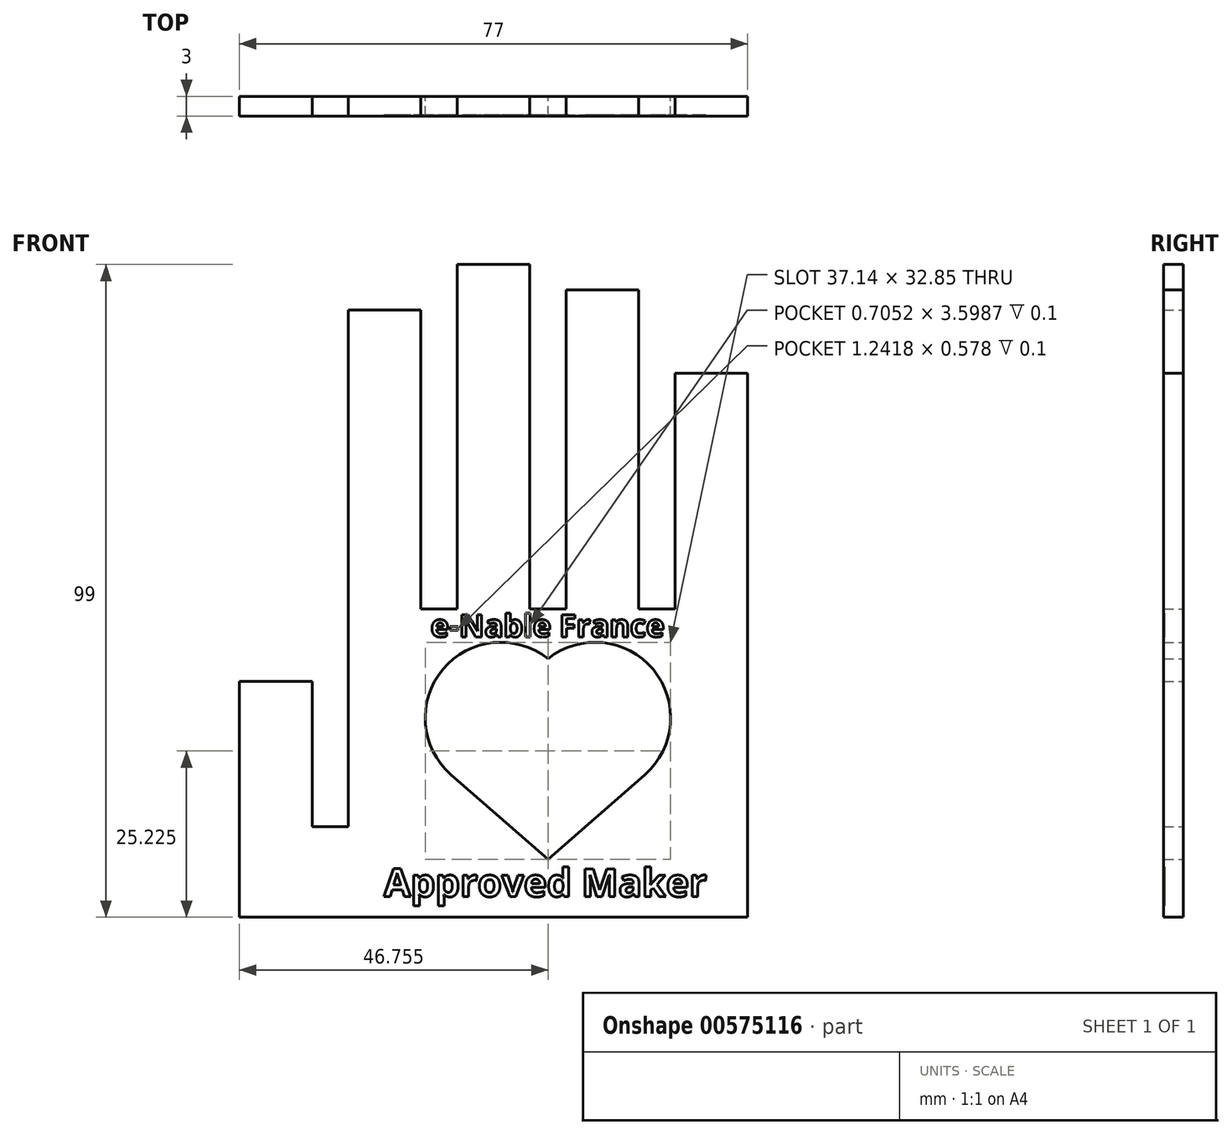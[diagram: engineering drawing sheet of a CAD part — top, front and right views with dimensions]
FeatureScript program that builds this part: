
annotation { "Feature Type Name" : "Feature", "Feature Type Description" : "" }
export const myFeature = defineFeature(function(context is Context, id is Id, definition is map)
    precondition{}
    {
        {
            var Q0;
            Q0=qCreatedBy(makeId("Front.planeOp"),FACE);
            var sketch = newSketch(context, id + "F0", { "sketchPlane" : qUnion([Q0])});
            skLineSegment(sketch, "E0", {"start": v(-37.6, -22.52) * mm, "end": v(-26.6, -22.52) * mm});
            skLineSegment(sketch, "E1", {"start": v(-26.6, -22.52) * mm, "end": v(-26.6, -44.52) * mm});
            skLineSegment(sketch, "E2", {"start": v(-26.6, -44.52) * mm, "end": v(-21.1, -44.52) * mm});
            skLineSegment(sketch, "E3", {"start": v(-21.1, -44.52) * mm, "end": v(-21.1, 33.86) * mm});
            skLineSegment(sketch, "E4", {"start": v(-21.1, 33.86) * mm, "end": v(-10.1, 33.86) * mm});
            skLineSegment(sketch, "E5", {"start": v(-10.1, 33.86) * mm, "end": v(-10.1, -11.52) * mm});
            skLineSegment(sketch, "E6", {"start": v(-10.1, -11.52) * mm, "end": v(-4.6, -11.52) * mm});
            skLineSegment(sketch, "E7", {"start": v(-4.6, -11.52) * mm, "end": v(-4.6, 40.73) * mm});
            skLineSegment(sketch, "E8", {"start": v(-4.6, 40.73) * mm, "end": v(6.4, 40.73) * mm});
            skLineSegment(sketch, "E9", {"start": v(6.4, 40.73) * mm, "end": v(6.4, -11.52) * mm});
            skLineSegment(sketch, "E10", {"start": v(6.4, -11.52) * mm, "end": v(11.9, -11.52) * mm});
            skLineSegment(sketch, "E11", {"start": v(11.9, -11.52) * mm, "end": v(11.9, 36.88) * mm});
            skLineSegment(sketch, "E12", {"start": v(11.9, 36.88) * mm, "end": v(22.9, 36.88) * mm});
            skLineSegment(sketch, "E13", {"start": v(22.9, 36.88) * mm, "end": v(22.9, -11.52) * mm});
            skLineSegment(sketch, "E14", {"start": v(22.9, -11.52) * mm, "end": v(28.4, -11.52) * mm});
            skLineSegment(sketch, "E15", {"start": v(28.4, -11.52) * mm, "end": v(28.4, 24.23) * mm});
            skLineSegment(sketch, "E16", {"start": v(28.4, 24.23) * mm, "end": v(39.4, 24.23) * mm});
            skLineSegment(sketch, "E17", {"start": v(39.4, 24.23) * mm, "end": v(39.4, -58.27) * mm});
            skLineSegment(sketch, "E18", {"start": v(39.4, -58.27) * mm, "end": v(-37.6, -58.27) * mm});
            skLineSegment(sketch, "E19", {"start": v(-37.6, -58.27) * mm, "end": v(-37.6, -22.52) * mm});
            skArc(sketch, "E20", {"start": v(9.15, -19.07) * mm, "mid": v(-6.78, -20.67) * mm, "end": v(-5.53, -36.64) * mm});
            skLineSegment(sketch, "E21", {"start": v(-5.53, -36.64) * mm, "end": v(9.15, -49.47) * mm});
            skLineSegment(sketch, "E22", {"start": v(9.15, 12.3) * mm, "end": v(9.15, -11.67) * mm, "construction": true});
            skArc(sketch, "E23.MirrorCS", {"start": v(9.15, -19.07) * mm, "mid": v(25.1, -20.67) * mm, "end": v(23.84, -36.64) * mm});
            skLineSegment(sketch, "E24.MirrorCS", {"start": v(23.84, -36.64) * mm, "end": v(9.15, -49.47) * mm});
            skSolve(sketch);
        }
        {
            var Q0;
            Q0=makeQuery(id+"F0.imprint","IMPRINT",FACE,{"disambiguationData":[TD([[makeQuery(id+"F0.imprint","IMPRINT",EDGE,{"derivedFrom":sQuery(id+"F0.wireOp",EDGE,"E0")}),-1.0]])]});
            extrude(context, id + "F1", {"entities" : qUnion([Q0]), "depth" : 3 * mm, "offsetDistance" : 25 * mm});
        }
        {
            var Q0;
            Q0=makeQuery(id+"F1.opExtrude","CAP_FACE",FACE,{"disambiguationData":[OSD([sQuery(id+"F0.wireOp",EDGE,"E0"),sQuery(id+"F0.wireOp",EDGE,"E1"),sQuery(id+"F0.wireOp",EDGE,"E2"),sQuery(id+"F0.wireOp",EDGE,"E3"),sQuery(id+"F0.wireOp",EDGE,"E4"),sQuery(id+"F0.wireOp",EDGE,"E5"),sQuery(id+"F0.wireOp",EDGE,"E6"),sQuery(id+"F0.wireOp",EDGE,"E7"),sQuery(id+"F0.wireOp",EDGE,"E8"),sQuery(id+"F0.wireOp",EDGE,"E9"),sQuery(id+"F0.wireOp",EDGE,"E10"),sQuery(id+"F0.wireOp",EDGE,"E11"),sQuery(id+"F0.wireOp",EDGE,"E12"),sQuery(id+"F0.wireOp",EDGE,"E13"),sQuery(id+"F0.wireOp",EDGE,"E14"),sQuery(id+"F0.wireOp",EDGE,"E15"),sQuery(id+"F0.wireOp",EDGE,"E16"),sQuery(id+"F0.wireOp",EDGE,"E17"),sQuery(id+"F0.wireOp",EDGE,"E18"),sQuery(id+"F0.wireOp",EDGE,"E19"),sQuery(id+"F0.wireOp",EDGE,"E20"),sQuery(id+"F0.wireOp",EDGE,"E21"),sQuery(id+"F0.wireOp",EDGE,"E23.MirrorCS"),sQuery(id+"F0.wireOp",EDGE,"E24.MirrorCS")])],"isStart":false});
            var sketch = newSketch(context, id + "F2", { "sketchPlane" : qUnion([Q0])});
            skText(sketch, "E25", { "text": "e-Nable France", "fontName": "NotoSans-Bold.ttf"});
            skText(sketch, "E26", { "text": "Approved Maker\n", "fontName": "NotoSans-Bold.ttf"});
            const initialGuessF2  = {"E25": [-0.00863, -0.01575, 1, 0, 0.00341], "E26": [-0.01573, -0.05514, 1, 0, 0.00425]};
            skSetInitialGuess(sketch, initialGuessF2);
            skSolve(sketch);
        }
        {
            var Q0;
            Q0=makeQuery(id+"F2.imprint","IMPRINT",FACE,{"disambiguationData":[TD([[makeQuery(id+"F2.imprint","IMPRINT",EDGE,{"derivedFrom":sQuery(id+"F2.wireOp",EDGE,"E25.sketch_text.stroke-0")}),-1.0]])]});
            var Q1;
            Q1=makeQuery(id+"F2.imprint","IMPRINT",FACE,{"disambiguationData":[TD([[makeQuery(id+"F2.imprint","IMPRINT",EDGE,{"derivedFrom":sQuery(id+"F2.wireOp",EDGE,"E25.sketch_text.stroke-20")}),-1.0]])]});
            var Q2;
            Q2=makeQuery(id+"F2.imprint","IMPRINT",FACE,{"disambiguationData":[TD([[makeQuery(id+"F2.imprint","IMPRINT",EDGE,{"derivedFrom":sQuery(id+"F2.wireOp",EDGE,"E25.sketch_text.stroke-24")}),-1.0]])]});
            var Q3;
            Q3=makeQuery(id+"F2.imprint","IMPRINT",FACE,{"disambiguationData":[TD([[makeQuery(id+"F2.imprint","IMPRINT",EDGE,{"derivedFrom":sQuery(id+"F2.wireOp",EDGE,"E25.sketch_text.stroke-38")}),-1.0]])]});
            var Q4;
            Q4=makeQuery(id+"F2.imprint","IMPRINT",FACE,{"disambiguationData":[TD([[makeQuery(id+"F2.imprint","IMPRINT",EDGE,{"derivedFrom":sQuery(id+"F2.wireOp",EDGE,"E25.sketch_text.stroke-63")}),-1.0]])]});
            var Q5;
            Q5=makeQuery(id+"F2.imprint","IMPRINT",FACE,{"disambiguationData":[TD([[makeQuery(id+"F2.imprint","IMPRINT",EDGE,{"derivedFrom":sQuery(id+"F2.wireOp",EDGE,"E25.sketch_text.stroke-86")}),-1.0]])]});
            var Q6;
            Q6=makeQuery(id+"F2.imprint","IMPRINT",FACE,{"disambiguationData":[TD([[makeQuery(id+"F2.imprint","IMPRINT",EDGE,{"derivedFrom":sQuery(id+"F2.wireOp",EDGE,"E25.sketch_text.stroke-90")}),-1.0]])]});
            var Q7;
            Q7=makeQuery(id+"F2.imprint","IMPRINT",FACE,{"disambiguationData":[TD([[makeQuery(id+"F2.imprint","IMPRINT",EDGE,{"derivedFrom":sQuery(id+"F2.wireOp",EDGE,"E25.sketch_text.stroke-110")}),-1.0]])]});
            var Q8;
            Q8=makeQuery(id+"F2.imprint","IMPRINT",FACE,{"disambiguationData":[TD([[makeQuery(id+"F2.imprint","IMPRINT",EDGE,{"derivedFrom":sQuery(id+"F2.wireOp",EDGE,"E25.sketch_text.stroke-120")}),-1.0]])]});
            var Q9;
            Q9=makeQuery(id+"F2.imprint","IMPRINT",FACE,{"disambiguationData":[TD([[makeQuery(id+"F2.imprint","IMPRINT",EDGE,{"derivedFrom":sQuery(id+"F2.wireOp",EDGE,"E25.sketch_text.stroke-133")}),-1.0]])]});
            var Q10;
            Q10=makeQuery(id+"F2.imprint","IMPRINT",FACE,{"disambiguationData":[TD([[makeQuery(id+"F2.imprint","IMPRINT",EDGE,{"derivedFrom":sQuery(id+"F2.wireOp",EDGE,"E25.sketch_text.stroke-158")}),-1.0]])]});
            var Q11;
            Q11=makeQuery(id+"F2.imprint","IMPRINT",FACE,{"disambiguationData":[TD([[makeQuery(id+"F2.imprint","IMPRINT",EDGE,{"derivedFrom":sQuery(id+"F2.wireOp",EDGE,"E25.sketch_text.stroke-175")}),-1.0]])]});
            var Q12;
            Q12=makeQuery(id+"F2.imprint","IMPRINT",FACE,{"disambiguationData":[TD([[makeQuery(id+"F2.imprint","IMPRINT",EDGE,{"derivedFrom":sQuery(id+"F2.wireOp",EDGE,"E25.sketch_text.stroke-189")}),-1.0]])]});
            extrude(context, id + "F3", {"entities" : qUnion([Q0, Q1, Q2, Q3, Q4, Q5, Q6, Q7, Q8, Q9, Q10, Q11, Q12]), "operationType" : NewBodyOperationType.REMOVE, "oppositeDirection" : true, "depth" : 0.1 * mm, "offsetDistance" : 25 * mm});
        }
        {
            var Q0;
            Q0=makeQuery(id+"F2.imprint","IMPRINT",FACE,{"disambiguationData":[TD([[makeQuery(id+"F2.imprint","IMPRINT",EDGE,{"derivedFrom":sQuery(id+"F2.wireOp",EDGE,"E26.sketch_text.stroke-0")}),-1.0]])]});
            var Q1;
            Q1=makeQuery(id+"F2.imprint","IMPRINT",FACE,{"disambiguationData":[TD([[makeQuery(id+"F2.imprint","IMPRINT",EDGE,{"derivedFrom":sQuery(id+"F2.wireOp",EDGE,"E26.sketch_text.stroke-12")}),-1.0]])]});
            var Q2;
            Q2=makeQuery(id+"F2.imprint","IMPRINT",FACE,{"disambiguationData":[TD([[makeQuery(id+"F2.imprint","IMPRINT",EDGE,{"derivedFrom":sQuery(id+"F2.wireOp",EDGE,"E26.sketch_text.stroke-35")}),-1.0]])]});
            var Q3;
            Q3=makeQuery(id+"F2.imprint","IMPRINT",FACE,{"disambiguationData":[TD([[makeQuery(id+"F2.imprint","IMPRINT",EDGE,{"derivedFrom":sQuery(id+"F2.wireOp",EDGE,"E26.sketch_text.stroke-58")}),-1.0]])]});
            var Q4;
            Q4=makeQuery(id+"F2.imprint","IMPRINT",FACE,{"disambiguationData":[TD([[makeQuery(id+"F2.imprint","IMPRINT",EDGE,{"derivedFrom":sQuery(id+"F2.wireOp",EDGE,"E26.sketch_text.stroke-71")}),-1.0]])]});
            var Q5;
            Q5=makeQuery(id+"F2.imprint","IMPRINT",FACE,{"disambiguationData":[TD([[makeQuery(id+"F2.imprint","IMPRINT",EDGE,{"derivedFrom":sQuery(id+"F2.wireOp",EDGE,"E26.sketch_text.stroke-89")}),-1.0]])]});
            var Q6;
            Q6=makeQuery(id+"F2.imprint","IMPRINT",FACE,{"disambiguationData":[TD([[makeQuery(id+"F2.imprint","IMPRINT",EDGE,{"derivedFrom":sQuery(id+"F2.wireOp",EDGE,"E26.sketch_text.stroke-99")}),-1.0]])]});
            var Q7;
            Q7=makeQuery(id+"F2.imprint","IMPRINT",FACE,{"disambiguationData":[TD([[makeQuery(id+"F2.imprint","IMPRINT",EDGE,{"derivedFrom":sQuery(id+"F2.wireOp",EDGE,"E26.sketch_text.stroke-119")}),-1.0]])]});
            var Q8;
            Q8=makeQuery(id+"F2.imprint","IMPRINT",FACE,{"disambiguationData":[TD([[makeQuery(id+"F2.imprint","IMPRINT",EDGE,{"derivedFrom":sQuery(id+"F2.wireOp",EDGE,"E26.sketch_text.stroke-142")}),-1.0]])]});
            var Q9;
            Q9=makeQuery(id+"F2.imprint","IMPRINT",FACE,{"disambiguationData":[TD([[makeQuery(id+"F2.imprint","IMPRINT",EDGE,{"derivedFrom":sQuery(id+"F2.wireOp",EDGE,"E26.sketch_text.stroke-161")}),-1.0]])]});
            var Q10;
            Q10=makeQuery(id+"F2.imprint","IMPRINT",FACE,{"disambiguationData":[TD([[makeQuery(id+"F2.imprint","IMPRINT",EDGE,{"derivedFrom":sQuery(id+"F2.wireOp",EDGE,"E26.sketch_text.stroke-186")}),-1.0]])]});
            var Q11;
            Q11=makeQuery(id+"F2.imprint","IMPRINT",FACE,{"disambiguationData":[TD([[makeQuery(id+"F2.imprint","IMPRINT",EDGE,{"derivedFrom":sQuery(id+"F2.wireOp",EDGE,"E26.sketch_text.stroke-201")}),-1.0]])]});
            var Q12;
            Q12=makeQuery(id+"F2.imprint","IMPRINT",FACE,{"disambiguationData":[TD([[makeQuery(id+"F2.imprint","IMPRINT",EDGE,{"derivedFrom":sQuery(id+"F2.wireOp",EDGE,"E26.sketch_text.stroke-221")}),-1.0]])]});
            extrude(context, id + "F4", {"entities" : qUnion([Q0, Q1, Q2, Q3, Q4, Q5, Q6, Q7, Q8, Q9, Q10, Q11, Q12]), "operationType" : NewBodyOperationType.REMOVE, "oppositeDirection" : true, "depth" : 0.2 * mm, "offsetDistance" : 25 * mm});
        }
    });
